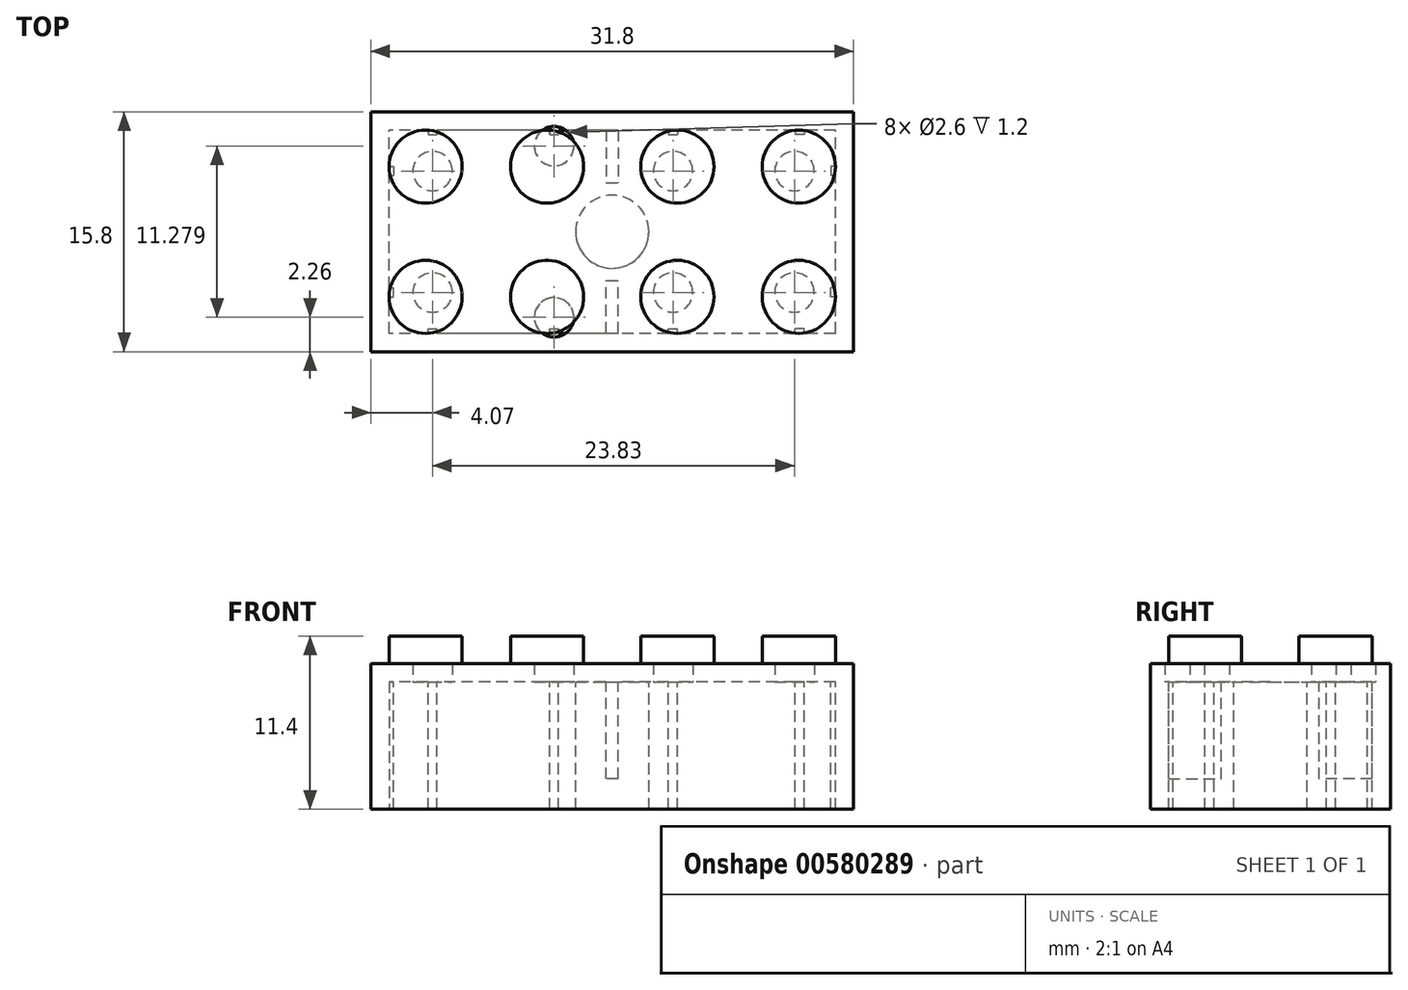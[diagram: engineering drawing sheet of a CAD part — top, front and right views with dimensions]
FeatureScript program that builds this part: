
annotation { "Feature Type Name" : "Feature", "Feature Type Description" : "" }
export const myFeature = defineFeature(function(context is Context, id is Id, definition is map)
    precondition{}
    {
        {
            var Q0;
            Q0=qCreatedBy(makeId("Top.planeOp"),FACE);
            var sketch = newSketch(context, id + "F0", { "sketchPlane" : qUnion([Q0])});
            skLineSegment(sketch, "E0.bottom", {"start": v(-15.9, 7.9) * mm, "end": v(15.9, 7.9) * mm});
            skLineSegment(sketch, "E0.top", {"start": v(-15.9, -7.9) * mm, "end": v(15.9, -7.9) * mm});
            skLineSegment(sketch, "E0.left", {"start": v(-15.9, 7.9) * mm, "end": v(-15.9, -7.9) * mm});
            skLineSegment(sketch, "E0.right", {"start": v(15.9, 7.9) * mm, "end": v(15.9, -7.9) * mm});
            skSolve(sketch);
        }
        {
            var Q0;
            Q0 = qSketchRegion(id + "F0", true);
            extrude(context, id + "F1", {"entities" : qUnion([Q0]), "endBound" : BoundingType.SYMMETRIC, "depth" : 9.6 * mm, "offsetDistance" : 25 * mm});
        }
        {
            var Q0;
            Q0=makeQuery(id+"F1.opExtrude","CAP_FACE",FACE,{"disambiguationData":[OSD([sQuery(id+"F0.wireOp",EDGE,"E0.bottom"),sQuery(id+"F0.wireOp",EDGE,"E0.top"),sQuery(id+"F0.wireOp",EDGE,"E0.left"),sQuery(id+"F0.wireOp",EDGE,"E0.right")])],"isStart":true});
            var sketch = newSketch(context, id + "F2", { "sketchPlane" : qUnion([Q0])});
            skLineSegment(sketch, "E1.bottom", {"start": v(14.7, 6.7) * mm, "end": v(-14.7, 6.7) * mm});
            skLineSegment(sketch, "E1.top", {"start": v(14.7, -6.7) * mm, "end": v(-14.7, -6.7) * mm});
            skLineSegment(sketch, "E1.left", {"start": v(14.7, 6.7) * mm, "end": v(14.7, -6.7) * mm});
            skLineSegment(sketch, "E1.right", {"start": v(-14.7, 6.7) * mm, "end": v(-14.7, -6.7) * mm});
            skPoint(sketch, "E1.middle", {"position": v(0, 0) * mm});
            skSolve(sketch);
        }
        {
            var Q0;
            Q0 = qSketchRegion(id + "F2", true);
            extrude(context, id + "F3", {"entities" : qUnion([Q0]), "operationType" : NewBodyOperationType.REMOVE, "oppositeDirection" : true, "depth" : 8.4 * mm, "offsetDistance" : 25 * mm});
        }
        {
            var Q0;
            Q0=makeQuery(id+"F1.opExtrude","CAP_FACE",FACE,{"disambiguationData":[OSD([sQuery(id+"F0.wireOp",EDGE,"E0.bottom"),sQuery(id+"F0.wireOp",EDGE,"E0.top"),sQuery(id+"F0.wireOp",EDGE,"E0.left"),sQuery(id+"F0.wireOp",EDGE,"E0.right")])],"isStart":false});
            var sketch = newSketch(context, id + "F4", { "sketchPlane" : qUnion([Q0])});
            skPoint(sketch, "E2.startSnap0", {"position": v(-15.9, 0) * mm});
            skLineSegment(sketch, "E3", {"start": v(-7.9, 7.9) * mm, "end": v(-7.9, -7.9) * mm, "construction": true});
            skLineSegment(sketch, "E4", {"start": v(7.9, 7.9) * mm, "end": v(7.9, -7.9) * mm, "construction": true});
            skLineSegment(sketch, "E5", {"start": v(0, 7.9) * mm, "end": v(0, -7.9) * mm, "construction": true});
            skLineSegment(sketch, "E6", {"start": v(-14.7, 7.9) * mm, "end": v(-14.7, -7.9) * mm, "construction": true});
            skLineSegment(sketch, "E7", {"start": v(14.7, 7.9) * mm, "end": v(14.7, -7.9) * mm, "construction": true});
            skCircle(sketch, "E8", {"center": v(-12.3, 4.3) * mm, "radius": 2.4 * mm});
            skLineSegment(sketch, "E9", {"start": v(-15.9, 6.7) * mm, "end": v(15.9, 6.7) * mm, "construction": true});
            skPoint(sketch, "E10", {"position": v(-12.27, 6.7) * mm});
            skPoint(sketch, "E11", {"position": v(-14.7, 4.3) * mm});
            skCircle(sketch, "E12.MirrorC", {"center": v(12.3, 4.3) * mm, "radius": 2.4 * mm});
            skCircle(sketch, "E13.MirrorC", {"center": v(-12.3, -4.3) * mm, "radius": 2.4 * mm});
            skCircle(sketch, "E14.MirrorC", {"center": v(12.3, -4.3) * mm, "radius": 2.4 * mm});
            skLineSegment(sketch, "E15", {"start": v(-12.3, 4.3) * mm, "end": v(-4.3, 4.3) * mm, "construction": true});
            skPoint(sketch, "E16", {"position": v(-4.3, 4.3) * mm});
            skCircle(sketch, "E17", {"center": v(-4.3, 4.3) * mm, "radius": 2.4 * mm});
            skCircle(sketch, "E18.MirrorC", {"center": v(4.3, 4.3) * mm, "radius": 2.4 * mm});
            skCircle(sketch, "E19.MirrorC", {"center": v(-4.3, -4.3) * mm, "radius": 2.4 * mm});
            skCircle(sketch, "E20.MirrorC", {"center": v(4.3, -4.3) * mm, "radius": 2.4 * mm});
            skSolve(sketch);
        }
        {
            var Q0;
            Q0 = qSketchRegion(id + "F4", true);
            extrude(context, id + "F5", {"entities" : qUnion([Q0]), "operationType" : NewBodyOperationType.ADD, "depth" : 1.8 * mm, "offsetDistance" : 25 * mm});
        }
        {
            var Q0;
            Q0=makeQuery(id+"F3.boolean.opBoolean","COPY",FACE,{"derivedFrom":makeQuery(id+"F3.opExtrude","CAP_FACE",FACE,{"disambiguationData":[OSD([sQuery(id+"F2.wireOp",EDGE,"E1.bottom"),sQuery(id+"F2.wireOp",EDGE,"E1.top"),sQuery(id+"F2.wireOp",EDGE,"E1.left"),sQuery(id+"F2.wireOp",EDGE,"E1.right")])],"isStart":false})});
            var sketch = newSketch(context, id + "F6", { "sketchPlane" : qUnion([Q0])});
            skCircle(sketch, "E21", {"center": v(-11.83, 4) * mm, "radius": 1.3 * mm});
            skCircle(sketch, "E22", {"center": v(-3.83, 5.64) * mm, "radius": 1.3 * mm});
            skCircle(sketch, "E23", {"center": v(4, 4) * mm, "radius": 1.3 * mm});
            skCircle(sketch, "E24", {"center": v(12, 4) * mm, "radius": 1.3 * mm});
            skCircle(sketch, "E25.MirrorC", {"center": v(-11.83, -4) * mm, "radius": 1.3 * mm});
            skCircle(sketch, "E26.MirrorC", {"center": v(-3.83, -5.64) * mm, "radius": 1.3 * mm});
            skCircle(sketch, "E27.MirrorC", {"center": v(4, -4) * mm, "radius": 1.3 * mm});
            skCircle(sketch, "E28.MirrorC", {"center": v(12, -4) * mm, "radius": 1.3 * mm});
            skSolve(sketch);
        }
        {
            var Q0;
            Q0 = qSketchRegion(id + "F6", true);
            extrude(context, id + "F7", {"entities" : qUnion([Q0]), "operationType" : NewBodyOperationType.REMOVE, "oppositeDirection" : true, "depth" : 1.2 * mm, "offsetDistance" : 25 * mm});
        }
        {
            var Q0;
            Q0=makeQuery(id+"F3.boolean.opBoolean","COPY",FACE,{"derivedFrom":makeQuery(id+"F3.opExtrude","CAP_FACE",FACE,{"disambiguationData":[OSD([sQuery(id+"F2.wireOp",EDGE,"E1.bottom"),sQuery(id+"F2.wireOp",EDGE,"E1.top"),sQuery(id+"F2.wireOp",EDGE,"E1.left"),sQuery(id+"F2.wireOp",EDGE,"E1.right")])],"isStart":false})});
            var sketch = newSketch(context, id + "F8", { "sketchPlane" : qUnion([Q0])});
            skPoint(sketch, "E29", {"position": v(-11.83, 4) * mm});
            skPoint(sketch, "E30", {"position": v(-11.83, -4) * mm});
            skPoint(sketch, "E31", {"position": v(-3.83, -4) * mm});
            skPoint(sketch, "E32", {"position": v(4, 4) * mm});
            skPoint(sketch, "E33", {"position": v(4, -4) * mm});
            skPoint(sketch, "E34", {"position": v(12, -4) * mm});
            skPoint(sketch, "E35", {"position": v(12, 4) * mm});
            skCircle(sketch, "E36", {"center": v(0, 0) * mm, "radius": 2.4 * mm});
            skSolve(sketch);
        }
        {
            var Q0;
            Q0 = qSketchRegion(id + "F8", true);
            var Q1;
            Q1=makeQuery(id+"F1.opExtrude","CAP_FACE",FACE,{"disambiguationData":[OSD([sQuery(id+"F0.wireOp",EDGE,"E0.bottom"),sQuery(id+"F0.wireOp",EDGE,"E0.top"),sQuery(id+"F0.wireOp",EDGE,"E0.left"),sQuery(id+"F0.wireOp",EDGE,"E0.right")])],"isStart":true});
            extrude(context, id + "F9", {"entities" : qUnion([Q0]), "operationType" : NewBodyOperationType.ADD, "endBound" : BoundingType.UP_TO_SURFACE, "depth" : 25 * mm, "endBoundEntityFace" : qUnion([Q1]), "offsetDistance" : 25 * mm});
        }
        {
            var Q0;
            {var subQ0=sQuery(id+"F2.wireOp",EDGE,"E1.left");var subQ1=sQuery(id+"F2.wireOp",EDGE,"E1.bottom");var subQ2=sQuery(id+"F2.wireOp",EDGE,"E1.top");var subQ3=sQuery(id+"F2.wireOp",EDGE,"E1.right");Q0=makeQuery(id+"F9.boolean.opBoolean","SPLIT",FACE,{"disambiguationData":[TD([makeQuery(id+"F3.boolean.opBoolean","COPY",FACE,{"derivedFrom":makeQuery(id+"F3.opExtrude","SWEPT_FACE",FACE,{"disambiguationData":[OSD([subQ1])]})})])],"derivedFrom":makeQuery(id+"F3.boolean.opBoolean","COPY",FACE,{"derivedFrom":makeQuery(id+"F3.opExtrude","CAP_FACE",FACE,{"disambiguationData":[OSD([subQ1,subQ2,subQ0,subQ3])],"isStart":false})})});}
            var sketch = newSketch(context, id + "F10", { "sketchPlane" : qUnion([Q0])});
            skPoint(sketch, "E37", {"position": v(-11.83, 4) * mm});
            skLineSegment(sketch, "E38", {"start": v(-11.83, 4) * mm, "end": v(-25.3, 4) * mm, "construction": true});
            skLineSegment(sketch, "E39.bottom", {"start": v(-14.7, 4.3) * mm, "end": v(-14.4, 4.3) * mm});
            skLineSegment(sketch, "E39.top", {"start": v(-14.7, 3.7) * mm, "end": v(-14.4, 3.7) * mm});
            skLineSegment(sketch, "E39.left", {"start": v(-14.7, 4.3) * mm, "end": v(-14.7, 3.7) * mm});
            skLineSegment(sketch, "E39.right", {"start": v(-14.4, 4.3) * mm, "end": v(-14.4, 3.7) * mm});
            skLineSegment(sketch, "E40.MirrorCS", {"start": v(-14.7, -4.3) * mm, "end": v(-14.4, -4.3) * mm});
            skLineSegment(sketch, "E41.MirrorCS", {"start": v(-14.4, -4.3) * mm, "end": v(-14.4, -3.7) * mm});
            skLineSegment(sketch, "E42.MirrorCS", {"start": v(-14.7, -4.3) * mm, "end": v(-14.7, -3.7) * mm});
            skLineSegment(sketch, "E43.MirrorCS", {"start": v(-14.7, -3.7) * mm, "end": v(-14.4, -3.7) * mm});
            skLineSegment(sketch, "E44.MirrorCS", {"start": v(14.7, 4.3) * mm, "end": v(14.4, 4.3) * mm});
            skLineSegment(sketch, "E45.MirrorCS", {"start": v(14.4, 4.3) * mm, "end": v(14.4, 3.7) * mm});
            skLineSegment(sketch, "E46.MirrorCS", {"start": v(14.7, 4.3) * mm, "end": v(14.7, 3.7) * mm});
            skLineSegment(sketch, "E47.MirrorCS", {"start": v(14.7, -3.7) * mm, "end": v(14.4, -3.7) * mm});
            skLineSegment(sketch, "E48.MirrorCS", {"start": v(14.4, -4.3) * mm, "end": v(14.4, -3.7) * mm});
            skLineSegment(sketch, "E49.MirrorCS", {"start": v(14.7, -4.3) * mm, "end": v(14.4, -4.3) * mm});
            skLineSegment(sketch, "E50.MirrorCS", {"start": v(14.7, -4.3) * mm, "end": v(14.7, -3.7) * mm});
            skLineSegment(sketch, "E51.MirrorCS", {"start": v(14.7, 3.7) * mm, "end": v(14.4, 3.7) * mm});
            skSolve(sketch);
        }
        {
            var Q0;
            Q0 = qSketchRegion(id + "F10", true);
            var Q1;
            Q1=makeQuery(id+"F1.opExtrude","CAP_FACE",FACE,{"disambiguationData":[OSD([sQuery(id+"F0.wireOp",EDGE,"E0.bottom"),sQuery(id+"F0.wireOp",EDGE,"E0.top"),sQuery(id+"F0.wireOp",EDGE,"E0.left"),sQuery(id+"F0.wireOp",EDGE,"E0.right")])],"isStart":true});
            extrude(context, id + "F11", {"entities" : qUnion([Q0]), "operationType" : NewBodyOperationType.ADD, "endBound" : BoundingType.UP_TO_SURFACE, "depth" : 25 * mm, "endBoundEntityFace" : qUnion([Q1]), "offsetDistance" : 25 * mm});
        }
        {
            var Q0;
            {var subQ0=sQuery(id+"F2.wireOp",EDGE,"E1.left");var subQ1=sQuery(id+"F2.wireOp",EDGE,"E1.bottom");var subQ2=sQuery(id+"F2.wireOp",EDGE,"E1.top");var subQ3=sQuery(id+"F2.wireOp",EDGE,"E1.right");Q0=makeQuery(id+"F9.boolean.opBoolean","SPLIT",FACE,{"disambiguationData":[TD([makeQuery(id+"F3.boolean.opBoolean","COPY",FACE,{"derivedFrom":makeQuery(id+"F3.opExtrude","SWEPT_FACE",FACE,{"disambiguationData":[OSD([subQ1])]})})])],"derivedFrom":makeQuery(id+"F3.boolean.opBoolean","COPY",FACE,{"derivedFrom":makeQuery(id+"F3.opExtrude","CAP_FACE",FACE,{"disambiguationData":[OSD([subQ1,subQ2,subQ0,subQ3])],"isStart":false})})});}
            var sketch = newSketch(context, id + "F12", { "sketchPlane" : qUnion([Q0])});
            skPoint(sketch, "E52", {"position": v(-11.83, 4) * mm});
            skLineSegment(sketch, "E53", {"start": v(-11.83, 4) * mm, "end": v(-11.83, 10.05) * mm, "construction": true});
            skLineSegment(sketch, "E54.bottom", {"start": v(-12.13, 6.7) * mm, "end": v(-11.53, 6.7) * mm});
            skLineSegment(sketch, "E54.top", {"start": v(-12.13, 6.4) * mm, "end": v(-11.53, 6.4) * mm});
            skLineSegment(sketch, "E54.left", {"start": v(-12.13, 6.7) * mm, "end": v(-12.13, 6.4) * mm});
            skLineSegment(sketch, "E54.right", {"start": v(-11.53, 6.7) * mm, "end": v(-11.53, 6.4) * mm});
            skPoint(sketch, "E55", {"position": v(-7.83, 0) * mm});
            skLineSegment(sketch, "E56", {"start": v(-7.83, 0) * mm, "end": v(-7.83, 7.65) * mm, "construction": true});
            skLineSegment(sketch, "E57.MirrorCS", {"start": v(-4.13, 6.7) * mm, "end": v(-4.13, 6.4) * mm});
            skLineSegment(sketch, "E58.MirrorCS", {"start": v(-3.53, 6.7) * mm, "end": v(-4.13, 6.7) * mm});
            skLineSegment(sketch, "E59.MirrorCS", {"start": v(-3.53, 6.7) * mm, "end": v(-3.53, 6.4) * mm});
            skLineSegment(sketch, "E60.MirrorCS", {"start": v(-3.53, 6.4) * mm, "end": v(-4.13, 6.4) * mm});
            skPoint(sketch, "E61", {"position": v(4, 4) * mm});
            skLineSegment(sketch, "E62", {"start": v(4, 4) * mm, "end": v(4, 7.54) * mm, "construction": true});
            skPoint(sketch, "E63", {"position": v(0, 0) * mm});
            skLineSegment(sketch, "E64.bottom", {"start": v(3.7, 6.7) * mm, "end": v(4.3, 6.7) * mm});
            skLineSegment(sketch, "E64.top", {"start": v(3.7, 6.4) * mm, "end": v(4.3, 6.4) * mm});
            skLineSegment(sketch, "E64.left", {"start": v(3.7, 6.7) * mm, "end": v(3.7, 6.4) * mm});
            skLineSegment(sketch, "E64.right", {"start": v(4.3, 6.7) * mm, "end": v(4.3, 6.4) * mm});
            skPoint(sketch, "E65", {"position": v(8.17, 0) * mm});
            skLineSegment(sketch, "E66", {"start": v(8.17, 0) * mm, "end": v(8.17, 6.9) * mm, "construction": true});
            skLineSegment(sketch, "E67.MirrorCS", {"start": v(12.64, 6.7) * mm, "end": v(12.64, 6.4) * mm});
            skLineSegment(sketch, "E68.MirrorCS", {"start": v(12.64, 6.7) * mm, "end": v(12.04, 6.7) * mm});
            skLineSegment(sketch, "E69.MirrorCS", {"start": v(12.64, 6.4) * mm, "end": v(12.04, 6.4) * mm});
            skLineSegment(sketch, "E70.MirrorCS", {"start": v(12.04, 6.7) * mm, "end": v(12.04, 6.4) * mm});
            skLineSegment(sketch, "E71.MirrorCS", {"start": v(-3.53, -6.7) * mm, "end": v(-4.13, -6.7) * mm});
            skLineSegment(sketch, "E72.MirrorCS", {"start": v(-3.53, -6.4) * mm, "end": v(-4.13, -6.4) * mm});
            skLineSegment(sketch, "E73.MirrorCS", {"start": v(-4.13, -6.7) * mm, "end": v(-4.13, -6.4) * mm});
            skLineSegment(sketch, "E74.MirrorCS", {"start": v(-3.53, -6.7) * mm, "end": v(-3.53, -6.4) * mm});
            skLineSegment(sketch, "E75.MirrorCS", {"start": v(-12.13, -6.7) * mm, "end": v(-12.13, -6.4) * mm});
            skLineSegment(sketch, "E76.MirrorCS", {"start": v(-12.13, -6.7) * mm, "end": v(-11.53, -6.7) * mm});
            skLineSegment(sketch, "E77.MirrorCS", {"start": v(-11.53, -6.7) * mm, "end": v(-11.53, -6.4) * mm});
            skLineSegment(sketch, "E78.MirrorCS", {"start": v(-12.13, -6.4) * mm, "end": v(-11.53, -6.4) * mm});
            skLineSegment(sketch, "E79.MirrorCS", {"start": v(3.7, -6.7) * mm, "end": v(3.7, -6.4) * mm});
            skLineSegment(sketch, "E80.MirrorCS", {"start": v(3.7, -6.7) * mm, "end": v(4.3, -6.7) * mm});
            skLineSegment(sketch, "E81.MirrorCS", {"start": v(4.3, -6.7) * mm, "end": v(4.3, -6.4) * mm});
            skLineSegment(sketch, "E82.MirrorCS", {"start": v(3.7, -6.4) * mm, "end": v(4.3, -6.4) * mm});
            skLineSegment(sketch, "E83.MirrorCS", {"start": v(12.64, -6.7) * mm, "end": v(12.04, -6.7) * mm});
            skLineSegment(sketch, "E84.MirrorCS", {"start": v(12.04, -6.7) * mm, "end": v(12.04, -6.4) * mm});
            skLineSegment(sketch, "E85.MirrorCS", {"start": v(12.64, -6.7) * mm, "end": v(12.64, -6.4) * mm});
            skLineSegment(sketch, "E86.MirrorCS", {"start": v(12.64, -6.4) * mm, "end": v(12.04, -6.4) * mm});
            skSolve(sketch);
        }
        {
            var Q0;
            Q0 = qSketchRegion(id + "F12", true);
            var Q1;
            {var subQ0=sQuery(id+"F0.wireOp",EDGE,"E0.right");var subQ1=sQuery(id+"F0.wireOp",EDGE,"E0.left");var subQ2=sQuery(id+"F0.wireOp",EDGE,"E0.top");var subQ3=sQuery(id+"F0.wireOp",EDGE,"E0.bottom");Q1=makeQuery(id+"F11.boolean.opBoolean","MERGE",FACE,{"derivedFrom":[makeQuery(id+"F1.opExtrude","CAP_FACE",FACE,{"disambiguationData":[OSD([subQ3,subQ2,subQ1,subQ0])],"isStart":true}),makeQuery(id+"F11.opExtrude","CAP_FACE",FACE,{"disambiguationData":[OSD([subQ3,subQ2,subQ1,subQ0]),OD(0.0)],"isStart":false}),makeQuery(id+"F11.opExtrude","CAP_FACE",FACE,{"disambiguationData":[OSD([subQ3,subQ2,subQ1,subQ0]),OD(1.0)],"isStart":false}),makeQuery(id+"F11.opExtrude","CAP_FACE",FACE,{"disambiguationData":[OSD([subQ3,subQ2,subQ1,subQ0]),OD(2.0)],"isStart":false}),makeQuery(id+"F11.opExtrude","CAP_FACE",FACE,{"disambiguationData":[OSD([subQ3,subQ2,subQ1,subQ0]),OD(3.0)],"isStart":false})]});}
            extrude(context, id + "F13", {"entities" : qUnion([Q0]), "operationType" : NewBodyOperationType.ADD, "endBound" : BoundingType.UP_TO_SURFACE, "depth" : 25 * mm, "endBoundEntityFace" : qUnion([Q1]), "offsetDistance" : 25 * mm});
        }
        {
            var Q0;
            {var subQ0=sQuery(id+"F2.wireOp",EDGE,"E1.left");var subQ1=sQuery(id+"F2.wireOp",EDGE,"E1.bottom");var subQ2=sQuery(id+"F2.wireOp",EDGE,"E1.top");var subQ3=sQuery(id+"F2.wireOp",EDGE,"E1.right");Q0=makeQuery(id+"F9.boolean.opBoolean","SPLIT",FACE,{"disambiguationData":[TD([makeQuery(id+"F3.boolean.opBoolean","COPY",FACE,{"derivedFrom":makeQuery(id+"F3.opExtrude","SWEPT_FACE",FACE,{"disambiguationData":[OSD([subQ1])]})})])],"derivedFrom":makeQuery(id+"F3.boolean.opBoolean","COPY",FACE,{"derivedFrom":makeQuery(id+"F3.opExtrude","CAP_FACE",FACE,{"disambiguationData":[OSD([subQ1,subQ2,subQ0,subQ3])],"isStart":false})})});}
            var sketch = newSketch(context, id + "F14", { "sketchPlane" : qUnion([Q0])});
            skLineSegment(sketch, "E87.bottom", {"start": v(-0.4, 6.7) * mm, "end": v(0.4, 6.7) * mm});
            skLineSegment(sketch, "E87.top", {"start": v(-0.4, 3.23) * mm, "end": v(0.4, 3.23) * mm});
            skLineSegment(sketch, "E87.left", {"start": v(-0.4, 6.7) * mm, "end": v(-0.4, 3.23) * mm});
            skLineSegment(sketch, "E87.right", {"start": v(0.4, 6.7) * mm, "end": v(0.4, 3.23) * mm});
            skLineSegment(sketch, "E88.MirrorCS", {"start": v(-0.4, -3.23) * mm, "end": v(0.4, -3.23) * mm});
            skLineSegment(sketch, "E89.MirrorCS", {"start": v(-0.4, -6.7) * mm, "end": v(-0.4, -3.23) * mm});
            skLineSegment(sketch, "E90.MirrorCS", {"start": v(0.4, -6.7) * mm, "end": v(0.4, -3.23) * mm});
            skLineSegment(sketch, "E91.MirrorCS", {"start": v(-0.4, -6.7) * mm, "end": v(0.4, -6.7) * mm});
            skSolve(sketch);
        }
        {
            var Q0;
            Q0 = qSketchRegion(id + "F14", true);
            extrude(context, id + "F15", {"entities" : qUnion([Q0]), "operationType" : NewBodyOperationType.ADD, "depth" : 6.4 * mm, "offsetDistance" : 25 * mm});
        }
    });
